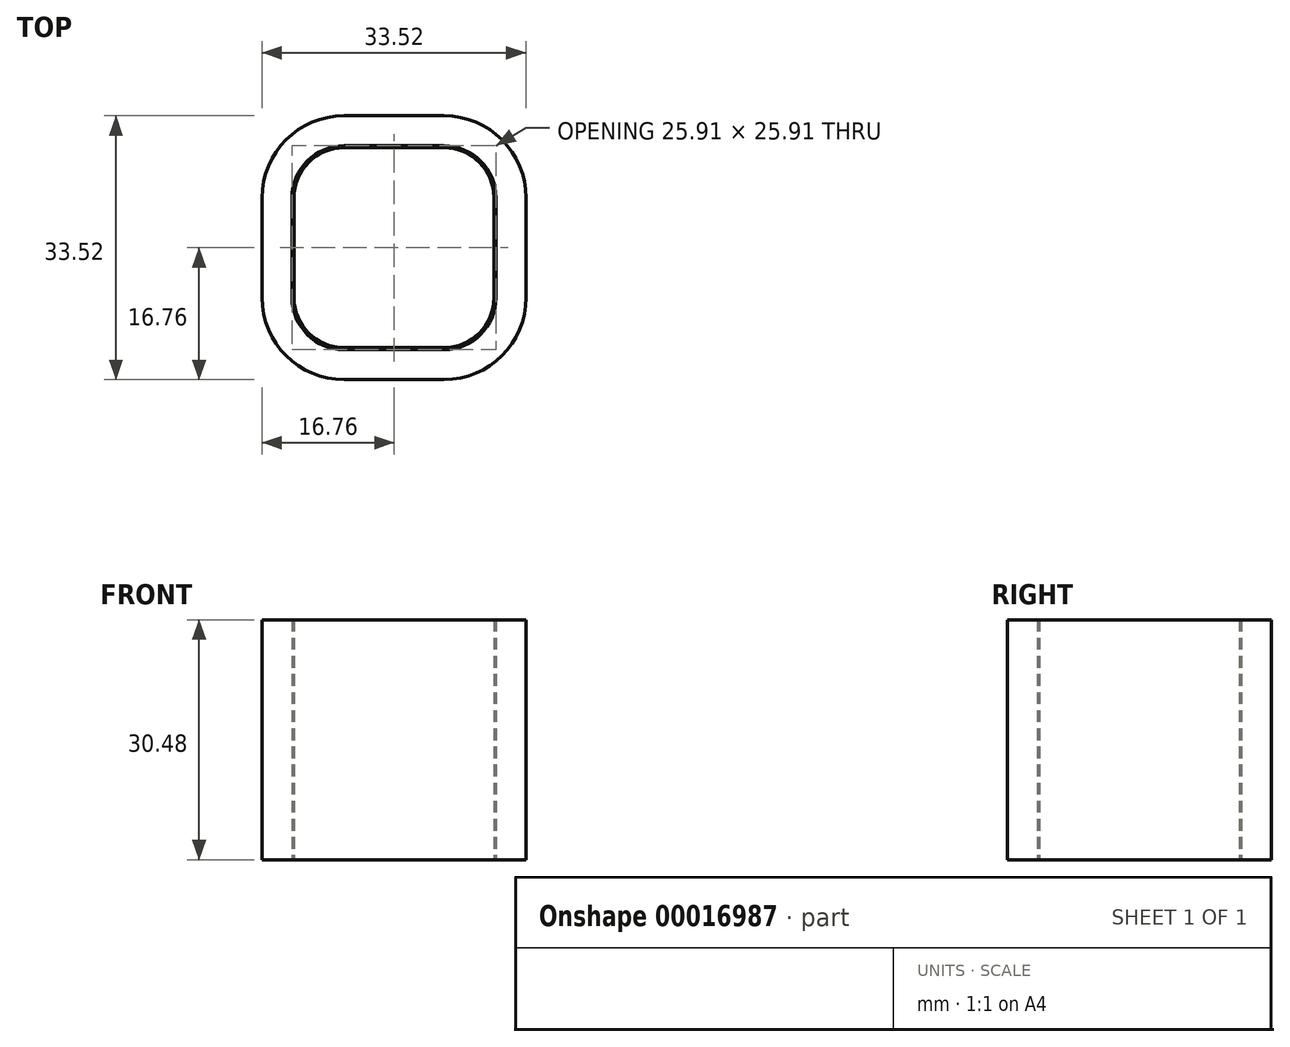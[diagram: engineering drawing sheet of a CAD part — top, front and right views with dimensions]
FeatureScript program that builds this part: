
annotation { "Feature Type Name" : "Feature", "Feature Type Description" : "" }
export const myFeature = defineFeature(function(context is Context, id is Id, definition is map)
    precondition{}
    {
        {
            var Q0;
            Q0=qCreatedBy(makeId("Top.planeOp"),FACE);
            var sketch = newSketch(context, id + "F0", { "sketchPlane" : qUnion([Q0])});
            skLineSegment(sketch, "E0.rect.bottom", {"start": v(6.35, 12.7) * mm, "end": v(-6.35, 12.7) * mm});
            skLineSegment(sketch, "E0.rect.top", {"start": v(6.35, -12.7) * mm, "end": v(-6.35, -12.7) * mm});
            skLineSegment(sketch, "E0.rect.left", {"start": v(12.7, 6.35) * mm, "end": v(12.7, -6.35) * mm});
            skLineSegment(sketch, "E0.rect.right", {"start": v(-12.7, 6.35) * mm, "end": v(-12.7, -6.35) * mm});
            skPoint(sketch, "E0.rect.middle", {"position": v(0, 0) * mm});
            skPoint(sketch, "E1.visualSharp", {"position": v(-12.7, 12.7) * mm});
            skArc(sketch, "E1.filletArc", {"start": v(-6.35, 12.7) * mm, "mid": v(-10.84, 10.84) * mm, "end": v(-12.7, 6.35) * mm});
            skPoint(sketch, "E2.visualSharp", {"position": v(-12.7, -12.7) * mm});
            skArc(sketch, "E2.filletArc", {"start": v(-12.7, -6.35) * mm, "mid": v(-10.84, -10.84) * mm, "end": v(-6.35, -12.7) * mm});
            skPoint(sketch, "E3.visualSharp", {"position": v(12.7, -12.7) * mm});
            skArc(sketch, "E3.filletArc", {"start": v(6.35, -12.7) * mm, "mid": v(10.84, -10.84) * mm, "end": v(12.7, -6.35) * mm});
            skPoint(sketch, "E4.visualSharp", {"position": v(12.7, 12.7) * mm});
            skArc(sketch, "E4.filletArc", {"start": v(12.7, 6.35) * mm, "mid": v(10.84, 10.84) * mm, "end": v(6.35, 12.7) * mm});
            skSolve(sketch);
        }
        {
            var Q0;
            Q0=qCreatedBy(makeId("Top.planeOp"),FACE);
            var sketch = newSketch(context, id + "F1", { "sketchPlane" : qUnion([Q0])});
            skLineSegment(sketch, "E5.0", {"start": v(12.95, -6.35) * mm, "end": v(12.95, 6.35) * mm});
            skArc(sketch, "E5.1", {"start": v(6.35, -12.95) * mm, "mid": v(11.02, -11.02) * mm, "end": v(12.95, -6.35) * mm});
            skLineSegment(sketch, "E5.2", {"start": v(-6.35, -12.95) * mm, "end": v(6.35, -12.95) * mm});
            skArc(sketch, "E5.3", {"start": v(-12.95, -6.35) * mm, "mid": v(-11.02, -11.02) * mm, "end": v(-6.35, -12.95) * mm});
            skLineSegment(sketch, "E5.4", {"start": v(-12.95, 6.35) * mm, "end": v(-12.95, -6.35) * mm});
            skArc(sketch, "E5.5", {"start": v(12.95, 6.35) * mm, "mid": v(11.02, 11.02) * mm, "end": v(6.35, 12.95) * mm});
            skArc(sketch, "E5.6", {"start": v(-6.35, 12.95) * mm, "mid": v(-11.02, 11.02) * mm, "end": v(-12.95, 6.35) * mm});
            skLineSegment(sketch, "E5.7", {"start": v(6.35, 12.95) * mm, "end": v(-6.35, 12.95) * mm});
            skLineSegment(sketch, "E6.0", {"start": v(16.76, -6.35) * mm, "end": v(16.76, 6.35) * mm});
            skArc(sketch, "E6.1", {"start": v(6.35, -16.76) * mm, "mid": v(13.71, -13.71) * mm, "end": v(16.76, -6.35) * mm});
            skLineSegment(sketch, "E6.2", {"start": v(-6.35, -16.76) * mm, "end": v(6.35, -16.76) * mm});
            skArc(sketch, "E6.3", {"start": v(-16.76, -6.35) * mm, "mid": v(-13.71, -13.71) * mm, "end": v(-6.35, -16.76) * mm});
            skLineSegment(sketch, "E6.4", {"start": v(-16.76, 6.35) * mm, "end": v(-16.76, -6.35) * mm});
            skArc(sketch, "E6.5", {"start": v(16.76, 6.35) * mm, "mid": v(13.71, 13.71) * mm, "end": v(6.35, 16.76) * mm});
            skArc(sketch, "E6.6", {"start": v(-6.35, 16.76) * mm, "mid": v(-13.71, 13.71) * mm, "end": v(-16.76, 6.35) * mm});
            skLineSegment(sketch, "E6.7", {"start": v(6.35, 16.76) * mm, "end": v(-6.35, 16.76) * mm});
            skSolve(sketch);
        }
        {
            var Q0;
            Q0=makeQuery(id+"F1.imprint","IMPRINT",FACE,{"disambiguationData":[TD([[makeQuery(id+"F1.imprint","IMPRINT",EDGE,{"derivedFrom":sQuery(id+"F1.wireOp",EDGE,"E5.0")}),-1.0]])]});
            extrude(context, id + "F2", {"entities" : qUnion([Q0]), "depth" : 30.48 * mm});
        }
        {
            var Q0;
            Q0=makeQuery(id+"F0.imprint","IMPRINT",FACE,{"disambiguationData":[TD([[makeQuery(id+"F0.imprint","IMPRINT",EDGE,{"derivedFrom":sQuery(id+"F0.wireOp",EDGE,"E0.rect.bottom")}),1.0]])]});
            extrude(context, id + "F3", {"entities" : qUnion([Q0]), "depth" : 30.48 * mm});
        }
    });
